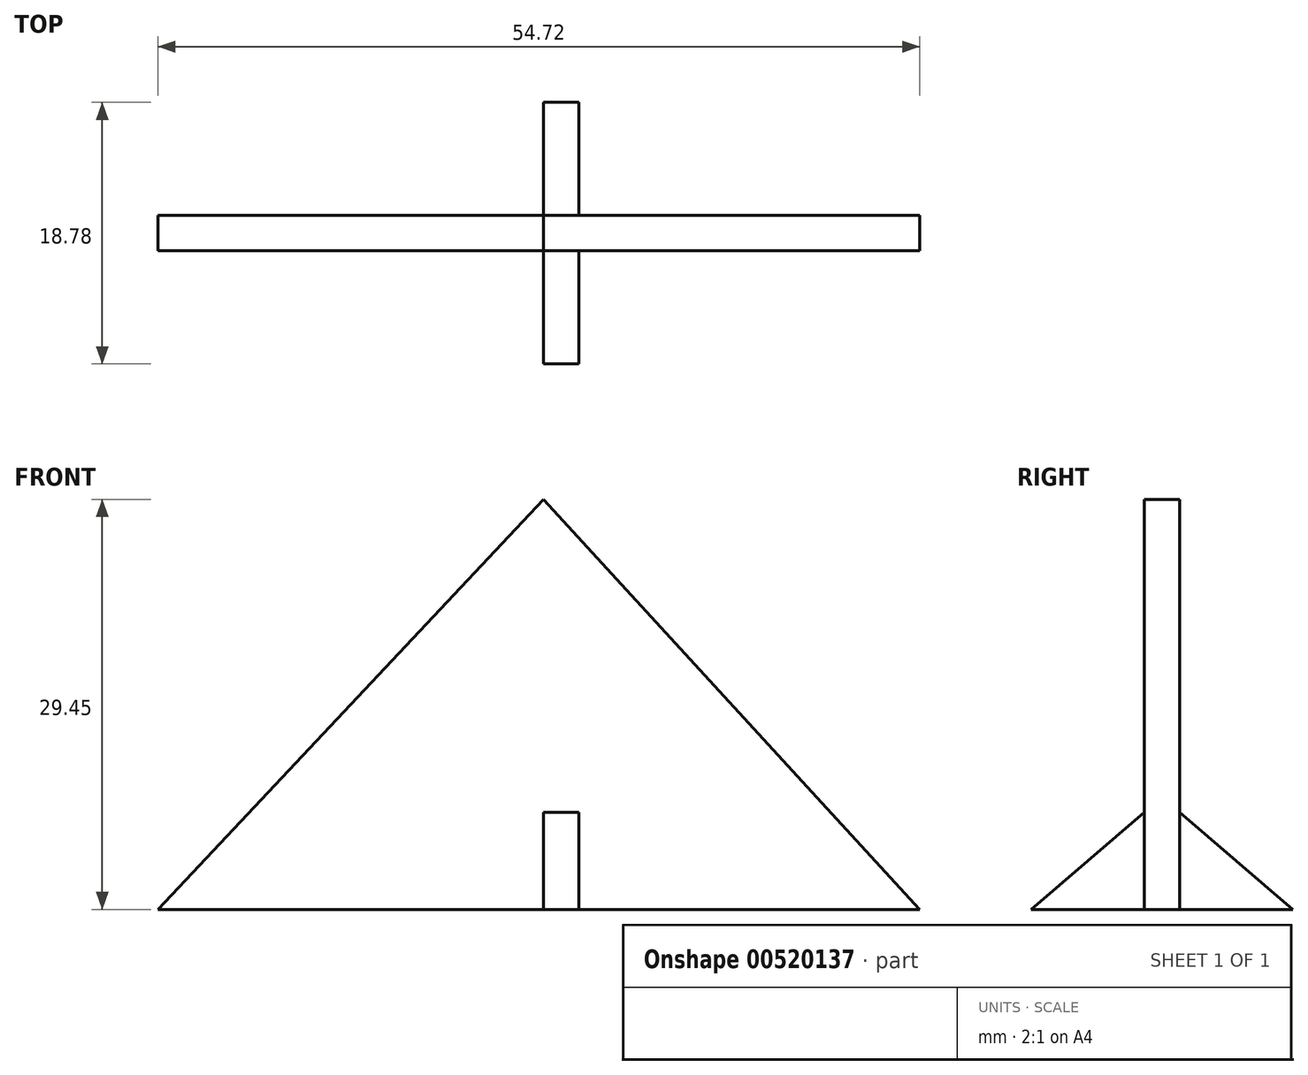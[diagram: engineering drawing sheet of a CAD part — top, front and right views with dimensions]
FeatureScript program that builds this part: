
annotation { "Feature Type Name" : "Feature", "Feature Type Description" : "" }
export const myFeature = defineFeature(function(context is Context, id is Id, definition is map)
    precondition{}
    {
        {
            var Q0;
            Q0=qCreatedBy(makeId("Front.planeOp"),FACE);
            var sketch = newSketch(context, id + "F0", { "sketchPlane" : qUnion([Q0])});
            skLineSegment(sketch, "E0", {"start": v(-27.7, 0) * mm, "end": v(27.02, 0) * mm});
            skLineSegment(sketch, "E1", {"start": v(0, 0) * mm, "end": v(0, 29.45) * mm});
            skLineSegment(sketch, "E2", {"start": v(0, 29.45) * mm, "end": v(27.02, 0) * mm});
            skLineSegment(sketch, "E3", {"start": v(0, 29.45) * mm, "end": v(-27.7, 0) * mm});
            skSolve(sketch);
        }
        {
            var Q0;
            Q0 = qSketchRegion(id + "F0", true);
            extrude(context, id + "F1", {"entities" : qUnion([Q0]), "endBound" : BoundingType.SYMMETRIC, "depth" : 2.54 * mm, "offsetDistance" : 25.4 * mm});
        }
        {
            var Q0;
            Q0=qCreatedBy(makeId("Right.planeOp"),FACE);
            var sketch = newSketch(context, id + "F2", { "sketchPlane" : qUnion([Q0])});
            skLineSegment(sketch, "E4", {"start": v(0, 8.06) * mm, "end": v(9.4, 0) * mm});
            skLineSegment(sketch, "E5", {"start": v(9.4, 0) * mm, "end": v(0, 0) * mm});
            skLineSegment(sketch, "E6", {"start": v(0, 0) * mm, "end": v(0, 8.06) * mm});
            skLineSegment(sketch, "E7.MirrorCS", {"start": v(-9.4, 0) * mm, "end": v(0, 0) * mm});
            skLineSegment(sketch, "E8.MirrorCS", {"start": v(0, 8.06) * mm, "end": v(-9.4, 0) * mm});
            skSolve(sketch);
        }
        {
            var Q0;
            Q0 = qSketchRegion(id + "F2", true);
            extrude(context, id + "F3", {"entities" : qUnion([Q0]), "operationType" : NewBodyOperationType.ADD, "depth" : 2.54 * mm, "offsetDistance" : 25.4 * mm});
        }
    });
